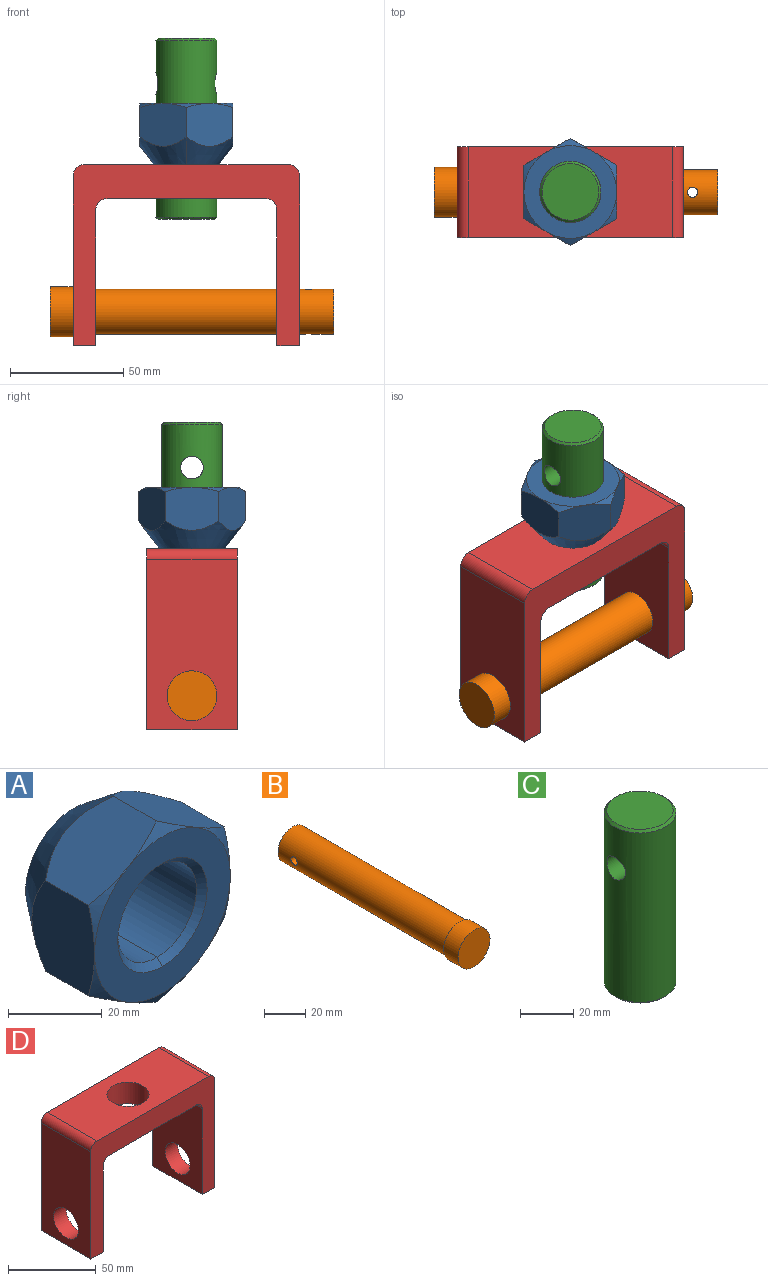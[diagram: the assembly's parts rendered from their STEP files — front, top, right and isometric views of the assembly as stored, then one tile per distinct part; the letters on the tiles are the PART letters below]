
ASSEMBLY  parts=4 mates=5
PART A: 22 faces, bbox 47.3x27x47.3 mm
  f0: plane 20.5x18.93mm, normal (-0.5,0,-0.87), area 399.7mm2, adj f1,f5,f6,f16,f17
  f1: plane 20.5x18.93mm, normal (0.5,0,-0.87), area 399.7mm2, adj f0,f2,f7,f16,f21
  f2: plane 23.67x18.93mm, normal (1,0,0), area 399.7mm2, adj f1,f3,f7,f20,f21
  f3: plane 20.5x18.93mm, normal (0.5,0,0.87), area 399.7mm2, adj f2,f4,f7,f19,f20
  f4: plane 20.5x18.93mm, normal (-0.5,0,0.87), area 399.7mm2, adj f3,f5,f6,f18,f19
  f5: plane 23.67x18.93mm, normal (-1,0,0), area 399.7mm2, adj f0,f4,f6,f17,f18
  f6: cone r=30.57mm half-angle=37.5deg, axis (0,-1,0), area 667.6mm2, adj f0,f4,f5,f7,f8
  f7: cone r=30.57mm half-angle=37.5deg, axis (0,-1,0), area 667.6mm2, adj f1,f2,f3,f6,f8
  f8: plane 28.6x28.6mm, normal (0,1,0), area 69.9mm2, adj f6,f7,f9,f10
  f9: cone r=13.5mm half-angle=45deg, axis (0,1,0), area 91.5mm2, adj f8,f10,f12
  f10: cone r=13.5mm half-angle=45deg, axis (0,1,0), area 91.5mm2, adj f8,f9,f11
  f11: cylinder r=11.88mm len=23.75mm, axis (0,1,0), area 886.2mm2, adj f10,f12,f14
  f12: cylinder r=11.88mm len=23.75mm, axis (0,1,0), area 886.2mm2, adj f9,f11,f13
  f13: cone r=11.88mm half-angle=45deg, axis (0,-1,0), area 91.5mm2, adj f12,f14,f15
  f14: cone r=11.88mm half-angle=45deg, axis (0,-1,0), area 91.5mm2, adj f11,f13,f15
  f15: plane 41x41mm, normal (0,-1,0), area 747.7mm2, adj f13,f14,f16,f17,f18,f19,f20,f21
  f16: cone r=20.5mm half-angle=60deg, axis (0,1,0), area 26.1mm2, adj f0,f1,f15
  f17: cone r=20.5mm half-angle=60deg, axis (0,1,0), area 26.1mm2, adj f0,f5,f15
  f18: cone r=20.5mm half-angle=60deg, axis (0,1,0), area 26.1mm2, adj f4,f5,f15
  f19: cone r=20.5mm half-angle=60deg, axis (0,1,0), area 26.1mm2, adj f3,f4,f15
  f20: cone r=20.5mm half-angle=60deg, axis (0,1,0), area 26.1mm2, adj f2,f3,f15
  f21: cone r=20.5mm half-angle=60deg, axis (0,1,0), area 26.1mm2, adj f1,f2,f15
PART B: 6 faces, bbox 22x125x22 mm
  f0: cylinder r=10mm len=115mm, axis (0,1,0), area 7193.6mm2, adj f3,f4,f5
  f1: cylinder r=11mm len=22mm, axis (0,1,0), area 691.2mm2, adj f2,f3
  f2: plane 22x22mm, normal (0,-1,0), area 380.1mm2, adj f1
  f3: plane 22x22mm, normal (0,1,0), area 66mm2, adj f0,f1
  f4: plane 20x20mm, normal (0,1,0), area 314.2mm2, adj f0
  f5: cylinder r=2.25mm len=20mm, axis (1,0,0), area 279.1mm2, adj f0
PART C: 6 faces, bbox 27x27x80 mm
  f0: cylinder r=13.5mm len=78mm, axis (0,0,-1), area 6456.3mm2, adj f3,f4,f5
  f1: plane 25x25mm, normal (0,0,1), area 490.9mm2, adj f5
  f2: plane 25x25mm, normal (0,0,-1), area 490.9mm2, adj f4
  f3: cylinder r=5mm len=27mm, axis (1,0,0), area 818.3mm2, adj f0
  f4: cone r=13.5mm half-angle=45deg, axis (0,0,1), area 115.5mm2, adj f0,f2
  f5: cone r=12.5mm half-angle=45deg, axis (0,0,-1), area 115.5mm2, adj f0,f1
PART D: 17 faces, bbox 100x40x80 mm
  f0: plane 40x10mm, normal (0,0,-1), area 400mm2, adj f1,f2,f5,f7
  f1: plane 100x80mm, normal (0,-1,0), area 2800mm2, adj f0,f3,f4,f5,f6,f7,f8,f9
  f2: plane 100x80mm, normal (0,1,0), area 2800mm2, adj f0,f3,f4,f5,f6,f7,f8,f9
  f3: plane 75x40mm, normal (1,0,0), area 2685.8mm2, adj f1,f2,f6,f12,f14
  f4: plane 90x40mm, normal (0,0,1), area 3147.6mm2, adj f1,f2,f12,f13,f16
  f5: plane 75x40mm, normal (-1,0,0), area 2685.8mm2, adj f0,f1,f2,f13,f15
  f6: plane 40x10mm, normal (0,0,-1), area 400mm2, adj f1,f2,f3,f8
  f7: plane 60x40mm, normal (1,0,0), area 2085.8mm2, adj f0,f1,f2,f11,f15
  f8: plane 60x40mm, normal (-1,0,0), area 2085.8mm2, adj f1,f2,f6,f10,f14
  f9: plane 70x40mm, normal (0,0,-1), area 2347.6mm2, adj f1,f2,f10,f11,f16
  f10: cylinder r=5mm len=40mm, axis (0,-1,0), area 314.2mm2, adj f1,f2,f8,f9
  f11: cylinder r=5mm len=40mm, axis (0,1,0), area 314.2mm2, adj f1,f2,f7,f9
  f12: cylinder r=5mm len=40mm, axis (0,-1,0), area 314.2mm2, adj f1,f2,f3,f4
  f13: cylinder r=5mm len=40mm, axis (0,1,0), area 314.2mm2, adj f1,f2,f4,f5
  f14: cylinder r=10mm len=20mm, axis (1,0,0), area 628.3mm2, adj f3,f8
  f15: cylinder r=10mm len=20mm, axis (1,0,0), area 628.3mm2, adj f5,f7
  f16: cylinder r=12mm len=24mm, axis (0,0,-1), area 1131mm2, adj f4,f9
PLACE A rot(axis=(-1,0,0),90deg) t=(-4,-18.66,20.49)mm
PLACE B rot(axis=(0.58,0.58,-0.58),120deg) t=(-1.5,-18.66,-71.51)mm
PLACE C t=(-4,-18.66,9.24)mm
PLACE D t=(-4,-18.66,-31.51)mm
MATE cylindrical C.f0 <-> D.f16  axis (0,0,-1) through (-4,-18.66,-29.76)mm
MATE planar B.f1 <-> D.f5  axis (1,0,0) through (-54,-18.66,-71.51)mm
MATE slider B.f0 <-> D.f14  axis (1,0,0) through (3.5,-18.66,-71.51)mm
MATE slider A.f6 <-> C.f0  axis (0,0,-1) through (-4,-18.66,6.99)mm
MATE planar A.f6 <-> D.f16  axis (0,0,-1) through (-4,-18.66,-6.51)mm
